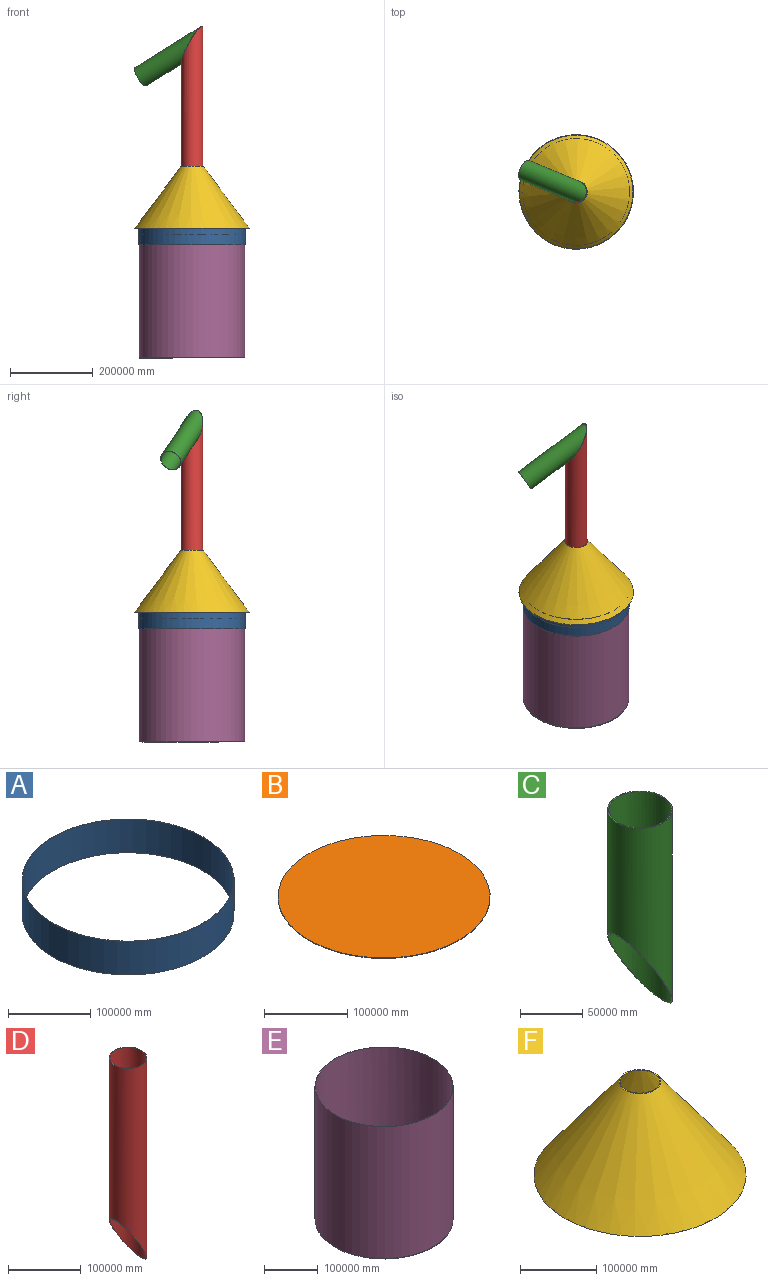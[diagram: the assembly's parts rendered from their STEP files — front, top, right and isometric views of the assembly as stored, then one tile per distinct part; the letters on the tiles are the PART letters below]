
ASSEMBLY  parts=6 mates=8
PART A: 4 faces, bbox 258000x258000x50000 mm
  f0: cylinder r=128500mm len=257000mm, axis (0,0,-1), area 40369465598.6mm2, adj f2,f3
  f1: cylinder r=129000mm len=258000mm, axis (0,0,-1), area 40526545231.3mm2, adj f2,f3
  f2: plane 258000x258000mm, normal (0,0,1), area 404480054.1mm2, adj f0,f1
  f3: plane 258000x258000mm, normal (0,0,-1), area 404480054.1mm2, adj f0,f1
PART B: 3 faces, bbox 255000x255000x800 mm
  f0: cylinder r=127500mm len=255000mm, axis (0,0,-1), area 640884901.3mm2, adj f1,f2
  f1: plane 255000x255000mm, normal (0,0,1), area 51070515574.9mm2, adj f0
  f2: plane 255000x255000mm, normal (0,0,-1), area 51070515574.9mm2, adj f0
PART C: 4 faces, bbox 52000x52000x200023.3 mm
  f0: cylinder r=25000mm len=198290.35mm, axis (0,0,-1), area 24342208825.8mm2, adj f2,f3
  f1: cylinder r=26000mm len=200023.3mm, axis (0,0,-1), area 25315901331mm2, adj f2,f3
  f2: plane 52000x52000mm, normal (0,0,1), area 160221225.3mm2, adj f0,f1
  f3: plane 90066.64x52000mm, normal (-0.87,0,-0.5), area 320442450.7mm2, adj f0,f1
PART D: 4 faces, bbox 52000x52000x350023.3 mm
  f0: cylinder r=25000mm len=348290.35mm, axis (0,0,-1), area 47904153727.7mm2, adj f2,f3
  f1: cylinder r=26000mm len=350023.3mm, axis (0,0,-1), area 49820324029mm2, adj f2,f3
  f2: plane 52000x52000mm, normal (0,0,1), area 160221225.3mm2, adj f0,f1
  f3: plane 90066.64x52000mm, normal (-0.87,0,-0.5), area 320442450.7mm2, adj f0,f1
PART E: 244 faces, bbox 256000x256000x300000 mm
  f0: cylinder r=127500mm len=300000mm, axis (0,0,-1), area 239531786728.4mm2, adj f2,f3,f4,f5,f6,f7,f8,f9
  f1: cylinder r=128000mm len=300000mm, axis (0,0,-1), area 241274315795.7mm2, adj f2,f3
  f2: plane 256000x256000mm, normal (0,0,1), area 401338461.5mm2, adj f0,f1
  f3: plane 256000x256000mm, normal (0,0,-1), area 4413642857.8mm2, adj f0,f1,f4,f5,f7,f8,f10,f11
  f4: plane 9802.04x5192.23mm, normal (0.88,-0.47,0), area 11092304.3mm2, adj f0,f3,f5,f6
  f5: plane 9998.08x4803.92mm, normal (-0.9,-0.43,0), area 11092304.3mm2, adj f0,f3,f4,f6
  f6: plane 10022.59x9996.16mm, normal (0,0,1), area 50153804.9mm2, adj f0,f4,f5
  f7: plane 10179.2x4407.17mm, normal (0.92,-0.4,0), area 11092304.3mm2, adj f0,f3,f8,f9
  f8: plane 9590.35x5573.55mm, normal (-0.86,-0.5,0), area 11092304.3mm2, adj f0,f3,f7,f9
  f9: plane 10179.2x9980.72mm, normal (0,0,1), area 50153804.9mm2, adj f0,f7,f8
  f10: plane 10493.6x3594.93mm, normal (0.95,-0.32,0), area 11092304.3mm2, adj f0,f3,f11,f12
  f11: plane 9123.49x6308.82mm, normal (-0.82,-0.57,0), area 11092304.3mm2, adj f0,f3,f10,f12
  f12: plane 10493.6x9903.75mm, normal (0,0,1), area 50153804.9mm2, adj f0,f10,f11
  f13: plane 10743.31x2760.53mm, normal (0.97,-0.25,0), area 11092304.3mm2, adj f0,f3,f14,f15
  f14: plane 8600.38x7005.19mm, normal (-0.78,-0.63,0), area 11092304.3mm2, adj f0,f3,f13,f15
  f15: plane 10743.31x9765.73mm, normal (0,0,1), area 50153804.9mm2, adj f0,f13,f14
  f16: plane 10926.78x1909.11mm, normal (0.99,-0.17,0), area 11092304.3mm2, adj f0,f3,f17,f18
  f17: plane 8024.24x7658.38mm, normal (-0.72,-0.69,0), area 11092304.3mm2, adj f0,f3,f16,f18
  f18: plane 10926.78x9567.49mm, normal (0,0,1), area 50153804.9mm2, adj f0,f16,f17
  f19: plane 11042.88x1045.92mm, normal (1,-0.09,0), area 11092304.3mm2, adj f0,f3,f20,f21
  f20: plane 8264.34x7398.64mm, normal (-0.67,-0.75,0), area 11092304.3mm2, adj f0,f3,f19,f21
  f21: plane 11042.88x9310.27mm, normal (0,0,1), area 50153804.9mm2, adj f0,f19,f20
  f22: plane 11090.9x1000mm, normal (1,-0.02,0), area 11092304.3mm2, adj f0,f3,f23,f24
  f23: plane 8819.36x6727.42mm, normal (-0.61,-0.8,0), area 11092304.3mm2, adj f0,f3,f22,f24
  f24: plane 11090.9x8995.64mm, normal (0,0,1), area 50153804.9mm2, adj f0,f22,f23
  f25: plane 11070.55x1000mm, normal (1,0.06,0), area 11092304.3mm2, adj f0,f3,f26,f27
  f26: plane 9320x6014.72mm, normal (-0.54,-0.84,0), area 11092304.3mm2, adj f0,f3,f25,f27
  f27: plane 11070.55x9320mm, normal (0,0,1), area 50153804.9mm2, adj f0,f25,f26
  f28: plane 10981.93x1560.89mm, normal (0.99,0.14,0), area 11092304.3mm2, adj f0,f3,f29,f30
  f29: plane 9763.18x5264.94mm, normal (-0.47,-0.88,0), area 11092304.3mm2, adj f0,f3,f28,f30
  f30: plane 10981.93x9763.18mm, normal (0,0,1), area 50153804.9mm2, adj f0,f28,f29
  f31: plane 10825.61x2417.71mm, normal (0.98,0.22,0), area 11092304.3mm2, adj f0,f3,f32,f33
  f32: plane 10146.16x4482.7mm, normal (-0.4,-0.91,0), area 11092304.3mm2, adj f0,f3,f31,f33
  f33: plane 10825.61x10146.16mm, normal (0,0,1), area 50153804.9mm2, adj f0,f31,f32
  f34: plane 10602.55x3259.62mm, normal (0.96,0.29,0), area 11092304.3mm2, adj f0,f3,f35,f36
  f35: plane 10466.59x3672.82mm, normal (-0.33,-0.94,0), area 11092304.3mm2, adj f0,f3,f34,f36
  f36: plane 10602.55x10466.59mm, normal (0,0,1), area 50153805mm2, adj f0,f34,f35
  f37: plane 10314.12x4081.44mm, normal (0.93,0.37,0), area 11092304.3mm2, adj f0,f3,f38,f39
  f38: plane 10722.5x2840.3mm, normal (-0.26,-0.97,0), area 11092304.3mm2, adj f0,f3,f37,f39
  f39: plane 10722.5x10314.12mm, normal (0,0,1), area 50153804.9mm2, adj f0,f37,f38
  f40: plane 9962.1x4878.1mm, normal (0.9,0.44,0), area 11092304.3mm2, adj f0,f3,f41,f42
  f41: plane 10912.29x1990.27mm, normal (-0.18,-0.98,0), area 11092304.3mm2, adj f0,f3,f40,f42
  f42: plane 10912.29x9962.1mm, normal (0,0,1), area 50153805mm2, adj f0,f40,f41
  f43: plane 9548.66x5644.68mm, normal (0.86,0.51,0), area 11092304.3mm2, adj f0,f3,f44,f45
  f44: plane 11034.8x1127.96mm, normal (-0.1,-0.99,0), area 11092304.3mm2, adj f0,f3,f43,f45
  f45: plane 11034.8x9548.66mm, normal (0,0,1), area 50153804.9mm2, adj f0,f43,f44
  f46: plane 9076.35x6376.45mm, normal (0.82,0.57,0), area 11092304.3mm2, adj f0,f3,f47,f48
  f47: plane 11089.29x1000mm, normal (-0.02,-1,0), area 11092304.3mm2, adj f0,f3,f46,f48
  f48: plane 11089.29x9076.35mm, normal (0,0,1), area 50153804.9mm2, adj f0,f46,f47
  f49: plane 8548.08x7068.92mm, normal (0.77,0.64,0), area 11092304.3mm2, adj f0,f3,f50,f51
  f50: plane 11075.4x1000mm, normal (0.06,-1,0), area 11092304.3mm2, adj f0,f3,f49,f51
  f51: plane 11075.4x9160.22mm, normal (0,0,1), area 50153804.9mm2, adj f0,f49,f50
  f52: plane 7967.1x7717.8mm, normal (0.72,0.7,0), area 11092304.3mm2, adj f0,f3,f53,f54
  f53: plane 10993.23x1479.23mm, normal (0.13,-0.99,0), area 11092304.3mm2, adj f0,f3,f52,f54
  f54: plane 10993.23x9446.33mm, normal (0,0,1), area 50153804.9mm2, adj f0,f52,f53
  f55: plane 8319.1x7337.01mm, normal (0.66,0.75,0), area 11092304.3mm2, adj f0,f3,f56,f57
  f56: plane 10843.28x2337.18mm, normal (0.21,-0.98,0), area 11092304.3mm2, adj f0,f3,f55,f57
  f57: plane 10843.28x9674.2mm, normal (0,0,1), area 50153804.9mm2, adj f0,f55,f56
  f58: plane 8869.11x6661.69mm, normal (0.6,0.8,0), area 11092304.3mm2, adj f0,f3,f59,f60
  f59: plane 10626.48x3180.73mm, normal (0.29,-0.96,0), area 11092304.3mm2, adj f0,f3,f58,f60
  f60: plane 10626.48x9842.42mm, normal (0,0,1), area 50153804.9mm2, adj f0,f58,f59
  f61: plane 9364.44x5945.29mm, normal (0.54,0.84,0), area 11092304.3mm2, adj f0,f3,f62,f63
  f62: plane 10344.17x4004.67mm, normal (0.36,-0.93,0), area 11092304.3mm2, adj f0,f3,f61,f63
  f63: plane 10344.17x9949.96mm, normal (0,0,1), area 50153804.9mm2, adj f0,f61,f62
  f64: plane 9802.04x5192.23mm, normal (0.47,0.88,0), area 11092304.3mm2, adj f0,f3,f65,f66
  f65: plane 9998.08x4803.92mm, normal (0.43,-0.9,0), area 11092304.3mm2, adj f0,f3,f64,f66
  f66: plane 10022.59x9996.16mm, normal (0,0,1), area 50153804.9mm2, adj f0,f64,f65
  f67: plane 10179.2x4407.17mm, normal (0.4,0.92,0), area 11092304.3mm2, adj f0,f3,f68,f69
  f68: plane 9590.35x5573.55mm, normal (0.5,-0.86,0), area 11092304.3mm2, adj f0,f3,f67,f69
  f69: plane 10179.2x9980.72mm, normal (0,0,1), area 50153804.9mm2, adj f0,f67,f68
  f70: plane 10493.6x3594.93mm, normal (0.32,0.95,0), area 11092304.3mm2, adj f0,f3,f71,f72
  f71: plane 9123.49x6308.82mm, normal (0.57,-0.82,0), area 11092304.3mm2, adj f0,f3,f70,f72
  f72: plane 10493.6x9903.75mm, normal (0,0,1), area 50153804.9mm2, adj f0,f70,f71
  f73: plane 10743.31x2760.53mm, normal (0.25,0.97,0), area 11092304.3mm2, adj f0,f3,f74,f75
  f74: plane 8600.38x7005.19mm, normal (0.63,-0.78,0), area 11092304.3mm2, adj f0,f3,f73,f75
  f75: plane 10743.31x9765.73mm, normal (0,0,1), area 50153804.9mm2, adj f0,f73,f74
  f76: plane 10926.78x1909.11mm, normal (0.17,0.99,0), area 11092304.3mm2, adj f0,f3,f77,f78
  f77: plane 8024.24x7658.38mm, normal (0.69,-0.72,0), area 11092304.3mm2, adj f0,f3,f76,f78
  f78: plane 10926.78x9567.49mm, normal (0,0,1), area 50153804.9mm2, adj f0,f76,f77
  f79: plane 11042.88x1045.92mm, normal (0.09,1,0), area 11092304.3mm2, adj f0,f3,f80,f81
  f80: plane 8264.34x7398.64mm, normal (0.75,-0.67,0), area 11092304.3mm2, adj f0,f3,f79,f81
  f81: plane 11042.88x9310.27mm, normal (0,0,1), area 50153804.9mm2, adj f0,f79,f80
  f82: plane 11090.9x1000mm, normal (0.02,1,0), area 11092304.3mm2, adj f0,f3,f83,f84
  f83: plane 8819.36x6727.42mm, normal (0.8,-0.61,0), area 11092304.3mm2, adj f0,f3,f82,f84
  f84: plane 11090.9x8995.64mm, normal (0,0,1), area 50153804.9mm2, adj f0,f82,f83
  f85: plane 11070.55x1000mm, normal (-0.06,1,0), area 11092304.3mm2, adj f0,f3,f86,f87
  f86: plane 9320x6014.72mm, normal (0.84,-0.54,0), area 11092304.3mm2, adj f0,f3,f85,f87
  f87: plane 11070.55x9320mm, normal (0,0,1), area 50153804.9mm2, adj f0,f85,f86
  f88: plane 10981.93x1560.89mm, normal (-0.14,0.99,0), area 11092304.3mm2, adj f0,f3,f89,f90
  f89: plane 9763.18x5264.94mm, normal (0.88,-0.47,0), area 11092304.3mm2, adj f0,f3,f88,f90
  f90: plane 10981.93x9763.18mm, normal (0,0,1), area 50153804.9mm2, adj f0,f88,f89
  f91: plane 10825.61x2417.71mm, normal (-0.22,0.98,0), area 11092304.3mm2, adj f0,f3,f92,f93
  f92: plane 10146.16x4482.7mm, normal (0.91,-0.4,0), area 11092304.3mm2, adj f0,f3,f91,f93
  f93: plane 10825.61x10146.16mm, normal (0,0,1), area 50153804.9mm2, adj f0,f91,f92
  f94: plane 10602.55x3259.62mm, normal (-0.29,0.96,0), area 11092304.3mm2, adj f0,f3,f95,f96
  f95: plane 10466.59x3672.82mm, normal (0.94,-0.33,0), area 11092304.3mm2, adj f0,f3,f94,f96
  f96: plane 10602.55x10466.59mm, normal (0,0,1), area 50153805mm2, adj f0,f94,f95
  f97: plane 10314.12x4081.44mm, normal (-0.37,0.93,0), area 11092304.3mm2, adj f0,f3,f98,f99
  f98: plane 10722.5x2840.3mm, normal (0.97,-0.26,0), area 11092304.3mm2, adj f0,f3,f97,f99
  f99: plane 10722.5x10314.12mm, normal (0,0,1), area 50153804.9mm2, adj f0,f97,f98
  f100: plane 9962.1x4878.1mm, normal (-0.44,0.9,0), area 11092304.3mm2, adj f0,f3,f101,f102
  f101: plane 10912.29x1990.27mm, normal (0.98,-0.18,0), area 11092304.3mm2, adj f0,f3,f100,f102
  f102: plane 10912.29x9962.1mm, normal (0,0,1), area 50153805mm2, adj f0,f100,f101
  f103: plane 9548.66x5644.68mm, normal (-0.51,0.86,0), area 11092304.3mm2, adj f0,f3,f104,f105
  f104: plane 11034.8x1127.96mm, normal (0.99,-0.1,0), area 11092304.3mm2, adj f0,f3,f103,f105
  f105: plane 11034.8x9548.66mm, normal (0,0,1), area 50153804.9mm2, adj f0,f103,f104
  f106: plane 9076.35x6376.45mm, normal (-0.57,0.82,0), area 11092304.3mm2, adj f0,f3,f107,f108
  f107: plane 11089.29x1000mm, normal (1,-0.02,0), area 11092304.3mm2, adj f0,f3,f106,f108
  f108: plane 11089.29x9076.35mm, normal (0,0,1), area 50153804.9mm2, adj f0,f106,f107
  f109: plane 8548.08x7068.92mm, normal (-0.64,0.77,0), area 11092304.3mm2, adj f0,f3,f110,f111
  f110: plane 11075.4x1000mm, normal (1,0.06,0), area 11092304.3mm2, adj f0,f3,f109,f111
  f111: plane 11075.4x9160.22mm, normal (0,0,1), area 50153804.9mm2, adj f0,f109,f110
  f112: plane 7967.1x7717.8mm, normal (-0.7,0.72,0), area 11092304.3mm2, adj f0,f3,f113,f114
  f113: plane 10993.23x1479.23mm, normal (0.99,0.13,0), area 11092304.3mm2, adj f0,f3,f112,f114
  f114: plane 10993.23x9446.33mm, normal (0,0,1), area 50153804.9mm2, adj f0,f112,f113
  f115: plane 8319.1x7337.01mm, normal (-0.75,0.66,0), area 11092304.3mm2, adj f0,f3,f116,f117
  f116: plane 10843.28x2337.18mm, normal (0.98,0.21,0), area 11092304.3mm2, adj f0,f3,f115,f117
  f117: plane 10843.28x9674.2mm, normal (0,0,1), area 50153804.9mm2, adj f0,f115,f116
  f118: plane 8869.11x6661.69mm, normal (-0.8,0.6,0), area 11092304.3mm2, adj f0,f3,f119,f120
  f119: plane 10626.48x3180.73mm, normal (0.96,0.29,0), area 11092304.3mm2, adj f0,f3,f118,f120
  f120: plane 10626.48x9842.42mm, normal (0,0,1), area 50153804.9mm2, adj f0,f118,f119
  f121: plane 9364.44x5945.29mm, normal (-0.84,0.54,0), area 11092304.3mm2, adj f0,f3,f122,f123
  f122: plane 10344.17x4004.67mm, normal (0.93,0.36,0), area 11092304.3mm2, adj f0,f3,f121,f123
  f123: plane 10344.17x9949.96mm, normal (0,0,1), area 50153804.9mm2, adj f0,f121,f122
  f124: plane 9802.04x5192.23mm, normal (-0.88,0.47,0), area 11092304.3mm2, adj f0,f3,f125,f126
  f125: plane 9998.08x4803.92mm, normal (0.9,0.43,0), area 11092304.3mm2, adj f0,f3,f124,f126
  f126: plane 10022.59x9996.16mm, normal (0,0,1), area 50153804.9mm2, adj f0,f124,f125
  f127: plane 10179.2x4407.17mm, normal (-0.92,0.4,0), area 11092304.3mm2, adj f0,f3,f128,f129
  f128: plane 9590.35x5573.55mm, normal (0.86,0.5,0), area 11092304.3mm2, adj f0,f3,f127,f129
  f129: plane 10179.2x9980.72mm, normal (0,0,1), area 50153804.9mm2, adj f0,f127,f128
  f130: plane 10493.6x3594.93mm, normal (-0.95,0.32,0), area 11092304.3mm2, adj f0,f3,f131,f132
  f131: plane 9123.49x6308.82mm, normal (0.82,0.57,0), area 11092304.3mm2, adj f0,f3,f130,f132
  f132: plane 10493.6x9903.75mm, normal (0,0,1), area 50153804.9mm2, adj f0,f130,f131
  f133: plane 10743.31x2760.53mm, normal (-0.97,0.25,0), area 11092304.3mm2, adj f0,f3,f134,f135
  f134: plane 8600.38x7005.19mm, normal (0.78,0.63,0), area 11092304.3mm2, adj f0,f3,f133,f135
  f135: plane 10743.31x9765.73mm, normal (0,0,1), area 50153804.9mm2, adj f0,f133,f134
  f136: plane 10926.78x1909.11mm, normal (-0.99,0.17,0), area 11092304.3mm2, adj f0,f3,f137,f138
  f137: plane 8024.24x7658.38mm, normal (0.72,0.69,0), area 11092304.3mm2, adj f0,f3,f136,f138
  f138: plane 10926.78x9567.49mm, normal (0,0,1), area 50153804.9mm2, adj f0,f136,f137
  f139: plane 11042.88x1045.92mm, normal (-1,0.09,0), area 11092304.3mm2, adj f0,f3,f140,f141
  f140: plane 8264.34x7398.64mm, normal (0.67,0.75,0), area 11092304.3mm2, adj f0,f3,f139,f141
  f141: plane 11042.88x9310.27mm, normal (0,0,1), area 50153804.9mm2, adj f0,f139,f140
  f142: plane 11090.9x1000mm, normal (-1,0.02,0), area 11092304.3mm2, adj f0,f3,f143,f144
  f143: plane 8819.36x6727.42mm, normal (0.61,0.8,0), area 11092304.3mm2, adj f0,f3,f142,f144
  f144: plane 11090.9x8995.64mm, normal (0,0,1), area 50153804.9mm2, adj f0,f142,f143
  f145: plane 11070.55x1000mm, normal (-1,-0.06,0), area 11092304.3mm2, adj f0,f3,f146,f147
  f146: plane 9320x6014.72mm, normal (0.54,0.84,0), area 11092304.3mm2, adj f0,f3,f145,f147
  f147: plane 11070.55x9320mm, normal (0,0,1), area 50153804.9mm2, adj f0,f145,f146
  f148: plane 10981.93x1560.89mm, normal (-0.99,-0.14,0), area 11092304.3mm2, adj f0,f3,f149,f150
  f149: plane 9763.18x5264.94mm, normal (0.47,0.88,0), area 11092304.3mm2, adj f0,f3,f148,f150
  f150: plane 10981.93x9763.18mm, normal (0,0,1), area 50153804.9mm2, adj f0,f148,f149
  f151: plane 10825.61x2417.71mm, normal (-0.98,-0.22,0), area 11092304.3mm2, adj f0,f3,f152,f153
  f152: plane 10146.16x4482.7mm, normal (0.4,0.91,0), area 11092304.3mm2, adj f0,f3,f151,f153
  f153: plane 10825.61x10146.16mm, normal (0,0,1), area 50153804.9mm2, adj f0,f151,f152
  f154: plane 10602.55x3259.62mm, normal (-0.96,-0.29,0), area 11092304.3mm2, adj f0,f3,f155,f156
  f155: plane 10466.59x3672.82mm, normal (0.33,0.94,0), area 11092304.3mm2, adj f0,f3,f154,f156
  f156: plane 10602.55x10466.59mm, normal (0,0,1), area 50153805mm2, adj f0,f154,f155
  f157: plane 10314.12x4081.44mm, normal (-0.93,-0.37,0), area 11092304.3mm2, adj f0,f3,f158,f159
  f158: plane 10722.5x2840.3mm, normal (0.26,0.97,0), area 11092304.3mm2, adj f0,f3,f157,f159
  f159: plane 10722.5x10314.12mm, normal (0,0,1), area 50153804.9mm2, adj f0,f157,f158
  f160: plane 9962.1x4878.1mm, normal (-0.9,-0.44,0), area 11092304.3mm2, adj f0,f3,f161,f162
  f161: plane 10912.29x1990.27mm, normal (0.18,0.98,0), area 11092304.3mm2, adj f0,f3,f160,f162
  f162: plane 10912.29x9962.1mm, normal (0,0,1), area 50153805mm2, adj f0,f160,f161
  f163: plane 9548.66x5644.68mm, normal (-0.86,-0.51,0), area 11092304.3mm2, adj f0,f3,f164,f165
  f164: plane 11034.8x1127.96mm, normal (0.1,0.99,0), area 11092304.3mm2, adj f0,f3,f163,f165
  f165: plane 11034.8x9548.66mm, normal (0,0,1), area 50153804.9mm2, adj f0,f163,f164
  f166: plane 9076.35x6376.45mm, normal (-0.82,-0.57,0), area 11092304.3mm2, adj f0,f3,f167,f168
  f167: plane 11089.29x1000mm, normal (0.02,1,0), area 11092304.3mm2, adj f0,f3,f166,f168
  f168: plane 11089.29x9076.35mm, normal (0,0,1), area 50153804.9mm2, adj f0,f166,f167
  f169: plane 8548.08x7068.92mm, normal (-0.77,-0.64,0), area 11092304.3mm2, adj f0,f3,f170,f171
  f170: plane 11075.4x1000mm, normal (-0.06,1,0), area 11092304.3mm2, adj f0,f3,f169,f171
  f171: plane 11075.4x9160.22mm, normal (0,0,1), area 50153804.9mm2, adj f0,f169,f170
  f172: plane 7967.1x7717.8mm, normal (-0.72,-0.7,0), area 11092304.3mm2, adj f0,f3,f173,f174
  f173: plane 10993.23x1479.23mm, normal (-0.13,0.99,0), area 11092304.3mm2, adj f0,f3,f172,f174
  f174: plane 10993.23x9446.33mm, normal (0,0,1), area 50153804.9mm2, adj f0,f172,f173
  f175: plane 8319.1x7337.01mm, normal (-0.66,-0.75,0), area 11092304.3mm2, adj f0,f3,f176,f177
  f176: plane 10843.28x2337.18mm, normal (-0.21,0.98,0), area 11092304.3mm2, adj f0,f3,f175,f177
  f177: plane 10843.28x9674.2mm, normal (0,0,1), area 50153804.9mm2, adj f0,f175,f176
  f178: plane 8869.11x6661.69mm, normal (-0.6,-0.8,0), area 11092304.3mm2, adj f0,f3,f179,f180
  f179: plane 10626.48x3180.73mm, normal (-0.29,0.96,0), area 11092304.3mm2, adj f0,f3,f178,f180
  f180: plane 10626.48x9842.42mm, normal (0,0,1), area 50153804.9mm2, adj f0,f178,f179
  f181: plane 9364.44x5945.29mm, normal (-0.54,-0.84,0), area 11092304.3mm2, adj f0,f3,f182,f183
  f182: plane 10344.17x4004.67mm, normal (-0.36,0.93,0), area 11092304.3mm2, adj f0,f3,f181,f183
  f183: plane 10344.17x9949.96mm, normal (0,0,1), area 50153804.9mm2, adj f0,f181,f182
  f184: plane 9802.04x5192.23mm, normal (-0.47,-0.88,0), area 11092304.3mm2, adj f0,f3,f185,f186
  f185: plane 9998.08x4803.92mm, normal (-0.43,0.9,0), area 11092304.3mm2, adj f0,f3,f184,f186
  f186: plane 10022.59x9996.16mm, normal (0,0,1), area 50153804.9mm2, adj f0,f184,f185
  f187: plane 10179.2x4407.17mm, normal (-0.4,-0.92,0), area 11092304.3mm2, adj f0,f3,f188,f189
  f188: plane 9590.35x5573.55mm, normal (-0.5,0.86,0), area 11092304.3mm2, adj f0,f3,f187,f189
  f189: plane 10179.2x9980.72mm, normal (0,0,1), area 50153804.9mm2, adj f0,f187,f188
  f190: plane 10493.6x3594.93mm, normal (-0.32,-0.95,0), area 11092304.3mm2, adj f0,f3,f191,f192
  f191: plane 9123.49x6308.82mm, normal (-0.57,0.82,0), area 11092304.3mm2, adj f0,f3,f190,f192
  f192: plane 10493.6x9903.75mm, normal (0,0,1), area 50153804.9mm2, adj f0,f190,f191
  f193: plane 10743.31x2760.53mm, normal (-0.25,-0.97,0), area 11092304.3mm2, adj f0,f3,f194,f195
  f194: plane 8600.38x7005.19mm, normal (-0.63,0.78,0), area 11092304.3mm2, adj f0,f3,f193,f195
  f195: plane 10743.31x9765.73mm, normal (0,0,1), area 50153804.9mm2, adj f0,f193,f194
  f196: plane 10926.78x1909.11mm, normal (-0.17,-0.99,0), area 11092304.3mm2, adj f0,f3,f197,f198
  f197: plane 8024.24x7658.38mm, normal (-0.69,0.72,0), area 11092304.3mm2, adj f0,f3,f196,f198
  f198: plane 10926.78x9567.49mm, normal (0,0,1), area 50153804.9mm2, adj f0,f196,f197
  f199: plane 11042.88x1045.92mm, normal (-0.09,-1,0), area 11092304.3mm2, adj f0,f3,f200,f201
  f200: plane 8264.34x7398.64mm, normal (-0.75,0.67,0), area 11092304.3mm2, adj f0,f3,f199,f201
  f201: plane 11042.88x9310.27mm, normal (0,0,1), area 50153804.9mm2, adj f0,f199,f200
  f202: plane 11090.9x1000mm, normal (-0.02,-1,0), area 11092304.3mm2, adj f0,f3,f203,f204
  f203: plane 8819.36x6727.42mm, normal (-0.8,0.61,0), area 11092304.3mm2, adj f0,f3,f202,f204
  f204: plane 11090.9x8995.64mm, normal (0,0,1), area 50153804.9mm2, adj f0,f202,f203
  f205: plane 11070.55x1000mm, normal (0.06,-1,0), area 11092304.3mm2, adj f0,f3,f206,f207
  f206: plane 9320x6014.72mm, normal (-0.84,0.54,0), area 11092304.3mm2, adj f0,f3,f205,f207
  f207: plane 11070.55x9320mm, normal (0,0,1), area 50153804.9mm2, adj f0,f205,f206
  f208: plane 10981.93x1560.89mm, normal (0.14,-0.99,0), area 11092304.3mm2, adj f0,f3,f209,f210
  f209: plane 9763.18x5264.94mm, normal (-0.88,0.47,0), area 11092304.3mm2, adj f0,f3,f208,f210
  f210: plane 10981.93x9763.18mm, normal (0,0,1), area 50153804.9mm2, adj f0,f208,f209
  f211: plane 10825.61x2417.71mm, normal (0.22,-0.98,0), area 11092304.3mm2, adj f0,f3,f212,f213
  f212: plane 10146.16x4482.7mm, normal (-0.91,0.4,0), area 11092304.3mm2, adj f0,f3,f211,f213
  f213: plane 10825.61x10146.16mm, normal (0,0,1), area 50153804.9mm2, adj f0,f211,f212
  f214: plane 10602.55x3259.62mm, normal (0.29,-0.96,0), area 11092304.3mm2, adj f0,f3,f215,f216
  f215: plane 10466.59x3672.82mm, normal (-0.94,0.33,0), area 11092304.3mm2, adj f0,f3,f214,f216
  f216: plane 10602.55x10466.59mm, normal (0,0,1), area 50153805mm2, adj f0,f214,f215
  f217: plane 10314.12x4081.44mm, normal (0.37,-0.93,0), area 11092304.3mm2, adj f0,f3,f218,f219
  f218: plane 10722.5x2840.3mm, normal (-0.97,0.26,0), area 11092304.3mm2, adj f0,f3,f217,f219
  f219: plane 10722.5x10314.12mm, normal (0,0,1), area 50153804.9mm2, adj f0,f217,f218
  f220: plane 9962.1x4878.1mm, normal (0.44,-0.9,0), area 11092304.3mm2, adj f0,f3,f221,f222
  f221: plane 10912.29x1990.27mm, normal (-0.98,0.18,0), area 11092304.3mm2, adj f0,f3,f220,f222
  f222: plane 10912.29x9962.1mm, normal (0,0,1), area 50153805mm2, adj f0,f220,f221
  f223: plane 9548.66x5644.68mm, normal (0.51,-0.86,0), area 11092304.3mm2, adj f0,f3,f224,f225
  f224: plane 11034.8x1127.96mm, normal (-0.99,0.1,0), area 11092304.3mm2, adj f0,f3,f223,f225
  f225: plane 11034.8x9548.66mm, normal (0,0,1), area 50153804.9mm2, adj f0,f223,f224
  f226: plane 9076.35x6376.45mm, normal (0.57,-0.82,0), area 11092304.3mm2, adj f0,f3,f227,f228
  f227: plane 11089.29x1000mm, normal (-1,0.02,0), area 11092304.3mm2, adj f0,f3,f226,f228
  f228: plane 11089.29x9076.35mm, normal (0,0,1), area 50153804.9mm2, adj f0,f226,f227
  f229: plane 8548.08x7068.92mm, normal (0.64,-0.77,0), area 11092304.3mm2, adj f0,f3,f230,f231
  f230: plane 11075.4x1000mm, normal (-1,-0.06,0), area 11092304.3mm2, adj f0,f3,f229,f231
  f231: plane 11075.4x9160.22mm, normal (0,0,1), area 50153804.9mm2, adj f0,f229,f230
  f232: plane 7967.1x7717.8mm, normal (0.7,-0.72,0), area 11092304.3mm2, adj f0,f3,f233,f234
  f233: plane 10993.23x1479.23mm, normal (-0.99,-0.13,0), area 11092304.3mm2, adj f0,f3,f232,f234
  f234: plane 10993.23x9446.33mm, normal (0,0,1), area 50153804.9mm2, adj f0,f232,f233
  f235: plane 8319.1x7337.01mm, normal (0.75,-0.66,0), area 11092304.3mm2, adj f0,f3,f236,f237
  f236: plane 10843.28x2337.18mm, normal (-0.98,-0.21,0), area 11092304.3mm2, adj f0,f3,f235,f237
  f237: plane 10843.28x9674.2mm, normal (0,0,1), area 50153804.9mm2, adj f0,f235,f236
  f238: plane 8869.11x6661.69mm, normal (0.8,-0.6,0), area 11092304.3mm2, adj f0,f3,f239,f240
  f239: plane 10626.48x3180.73mm, normal (-0.96,-0.29,0), area 11092304.3mm2, adj f0,f3,f238,f240
  f240: plane 10626.48x9842.42mm, normal (0,0,1), area 50153804.9mm2, adj f0,f238,f239
  f241: plane 9364.44x5945.29mm, normal (0.84,-0.54,0), area 11092304.3mm2, adj f0,f3,f242,f243
  f242: plane 10344.17x4004.67mm, normal (-0.93,-0.36,0), area 11092304.3mm2, adj f0,f3,f241,f243
  f243: plane 10344.17x9949.96mm, normal (0,0,1), area 50153804.9mm2, adj f0,f241,f242
PART F: 4 faces, bbox 277492x277492x150000 mm
  f0: plane 54492.02x54492.02mm, normal (0,0,1), area 208429398.1mm2, adj f1,f3
  f1: cone r=26000mm half-angle=36.6deg, axis (0,0,-1), area 96002138978.4mm2, adj f0,f2
  f2: plane 277492.02x277492.02mm, normal (0,0,-1), area 1081354046mm2, adj f1,f3
  f3: cone r=138746.01mm half-angle=36.6deg, axis (0,0,-1), area 97465377662.6mm2, adj f0,f2
PLACE A rot(axis=(0,0,1),67.5deg) t=(0,0,274285.58)mm
PLACE B rot(axis=(0,0,-1),178.5deg) t=(0,0,0)mm
PLACE C rot(axis=(-0.19,-0.97,-0.11),121.3deg) t=(36036.42,-14912.3,781768.92)mm
PLACE D rot(axis=(-0.98,0.19,0),180deg) t=(0,0,804285.58)mm
PLACE E rot(axis=(0,0,-1),18.8deg) t=(0,0,-200)mm
PLACE F rot(axis=(0,0,-1),22.5deg) t=(0,0,314285.58)mm
MATE fastened D.f0 <-> F.f1  axis (0,0,-1) through (0,0,454285.58)mm
MATE cylindrical E.f0 <-> B.f0  axis (0,0,-1) through (0,0,299800)mm
MATE cylindrical A.f1 <-> E.f1  axis (0,0,1) through (0,0,324285.58)mm
MATE fastened F.f1 <-> A.f1  axis (0,0,-1) through (0,0,314285.58)mm
MATE planar E.f36 <-> B.f0  axis (0,0,1) through (-52557.76,112470.53,800)mm
MATE fastened C.f3 <-> D.f3  axis (0.8,-0.33,-0.5) through (0,0,759252.26)mm
MATE cylindrical A.f1 <-> F.f1  axis (0,0,1) through (0,0,324285.58)mm
MATE cylindrical D.f0 <-> F.f1  axis (0,0,1) through (0,0,630335.58)mm
